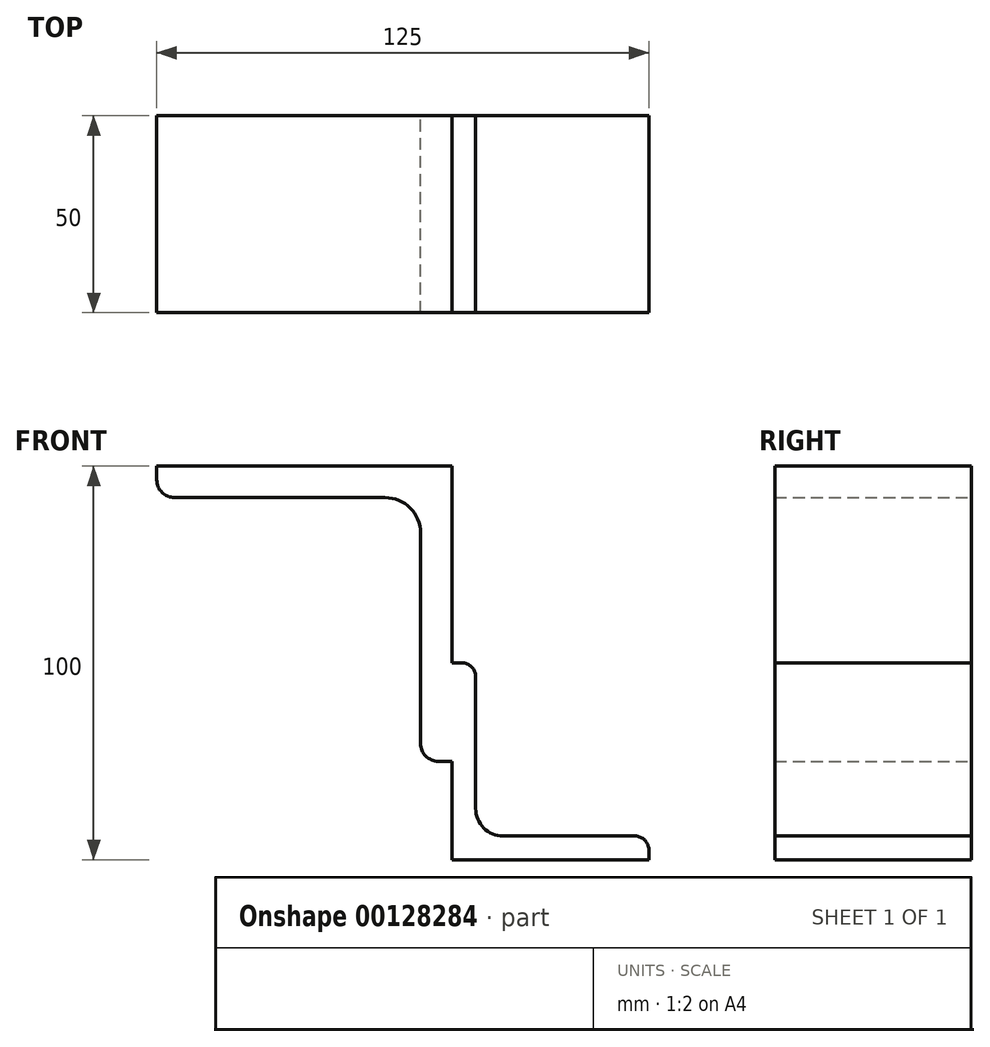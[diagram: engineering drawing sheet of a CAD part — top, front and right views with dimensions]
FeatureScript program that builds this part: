
annotation { "Feature Type Name" : "Feature", "Feature Type Description" : "" }
export const myFeature = defineFeature(function(context is Context, id is Id, definition is map)
    precondition{}
    {
        {
            var Q0;
            Q0=qCreatedBy(makeId("Front.planeOp"),FACE);
            var sketch = newSketch(context, id + "F0", { "sketchPlane" : qUnion([Q0])});
            skLineSegment(sketch, "E0", {"start": v(-75, 0) * mm, "end": v(0, 0) * mm});
            skLineSegment(sketch, "E1", {"start": v(0, 0) * mm, "end": v(0, -75) * mm});
            skLineSegment(sketch, "E2", {"start": v(0, -75) * mm, "end": v(-3.5, -75) * mm});
            skLineSegment(sketch, "E3", {"start": v(-8, -70.5) * mm, "end": v(-8, -17) * mm});
            skLineSegment(sketch, "E4", {"start": v(-17, -8) * mm, "end": v(-70.5, -8) * mm});
            skLineSegment(sketch, "E5", {"start": v(-75, -3.5) * mm, "end": v(-75, 0) * mm});
            skLineSegment(sketch, "E6", {"start": v(0, -50) * mm, "end": v(0, -100) * mm});
            skLineSegment(sketch, "E7", {"start": v(0, -100) * mm, "end": v(50, -100) * mm});
            skLineSegment(sketch, "E8", {"start": v(50, -100) * mm, "end": v(50, -97.5) * mm});
            skLineSegment(sketch, "E9", {"start": v(46.5, -94) * mm, "end": v(13, -94) * mm});
            skLineSegment(sketch, "E10", {"start": v(6, -87) * mm, "end": v(6, -53.5) * mm});
            skLineSegment(sketch, "E11", {"start": v(2.5, -50) * mm, "end": v(0, -50) * mm});
            skPoint(sketch, "E12.visualSharp", {"position": v(-8, -8) * mm});
            skArc(sketch, "E12.filletArc", {"start": v(-8, -17) * mm, "mid": v(-10.64, -10.64) * mm, "end": v(-17, -8) * mm});
            skPoint(sketch, "E13.visualSharp", {"position": v(-75, -8) * mm});
            skArc(sketch, "E13.filletArc", {"start": v(-75, -3.5) * mm, "mid": v(-73.68, -6.68) * mm, "end": v(-70.5, -8) * mm});
            skPoint(sketch, "E14.visualSharp", {"position": v(-8, -75) * mm});
            skArc(sketch, "E14.filletArc", {"start": v(-8, -70.5) * mm, "mid": v(-6.68, -73.68) * mm, "end": v(-3.5, -75) * mm});
            skPoint(sketch, "E15.visualSharp", {"position": v(6, -94) * mm});
            skArc(sketch, "E15.filletArc", {"start": v(6, -87) * mm, "mid": v(8.05, -91.95) * mm, "end": v(13, -94) * mm});
            skPoint(sketch, "E16.visualSharp", {"position": v(50, -94) * mm});
            skArc(sketch, "E16.filletArc", {"start": v(50, -97.5) * mm, "mid": v(48.97, -95.03) * mm, "end": v(46.5, -94) * mm});
            skPoint(sketch, "E17.visualSharp", {"position": v(6, -50) * mm});
            skArc(sketch, "E17.filletArc", {"start": v(6, -53.5) * mm, "mid": v(4.97, -51.03) * mm, "end": v(2.5, -50) * mm});
            skPoint(sketch, "E18", {"position": v(-30, 0) * mm});
            skSolve(sketch);
        }
        {
            var Q0;
            Q0 = qSketchRegion(id + "F0", true);
            extrude(context, id + "F1", {"entities" : qUnion([Q0]), "depth" : 50 * mm});
        }
    });
